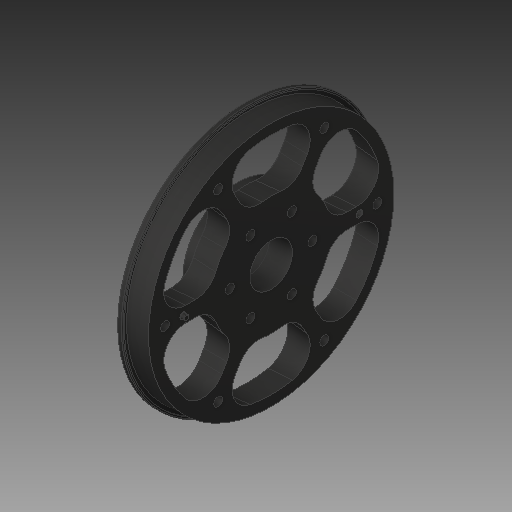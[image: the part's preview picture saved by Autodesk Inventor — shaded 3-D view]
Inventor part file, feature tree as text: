
AUTODESK INVENTOR PART (.ipt)
format: ipt  version: 2018 (Build 220112000, 112)  size: 1,159,680 bytes
history: native  units: in
note: dims shown in document units (in); Inventor stores cm internally (conversion verified against a paired STEP export)
features: revolve x1
ambient origin geometry x8: Origin, YZ Plane, XZ Plane, XY Plane, X Axis, Y Axis, Z Axis, Center Point
bodies: Solid1 (feature_tree)
feature tree (1):
  revolve  "Revolve3"  [1 undecoded]
note: 1 required parameter value undecoded (feature->parameter linkage not recoverable at this tier; creation-order binding heuristic only, values carry confidence <= 0.55)
